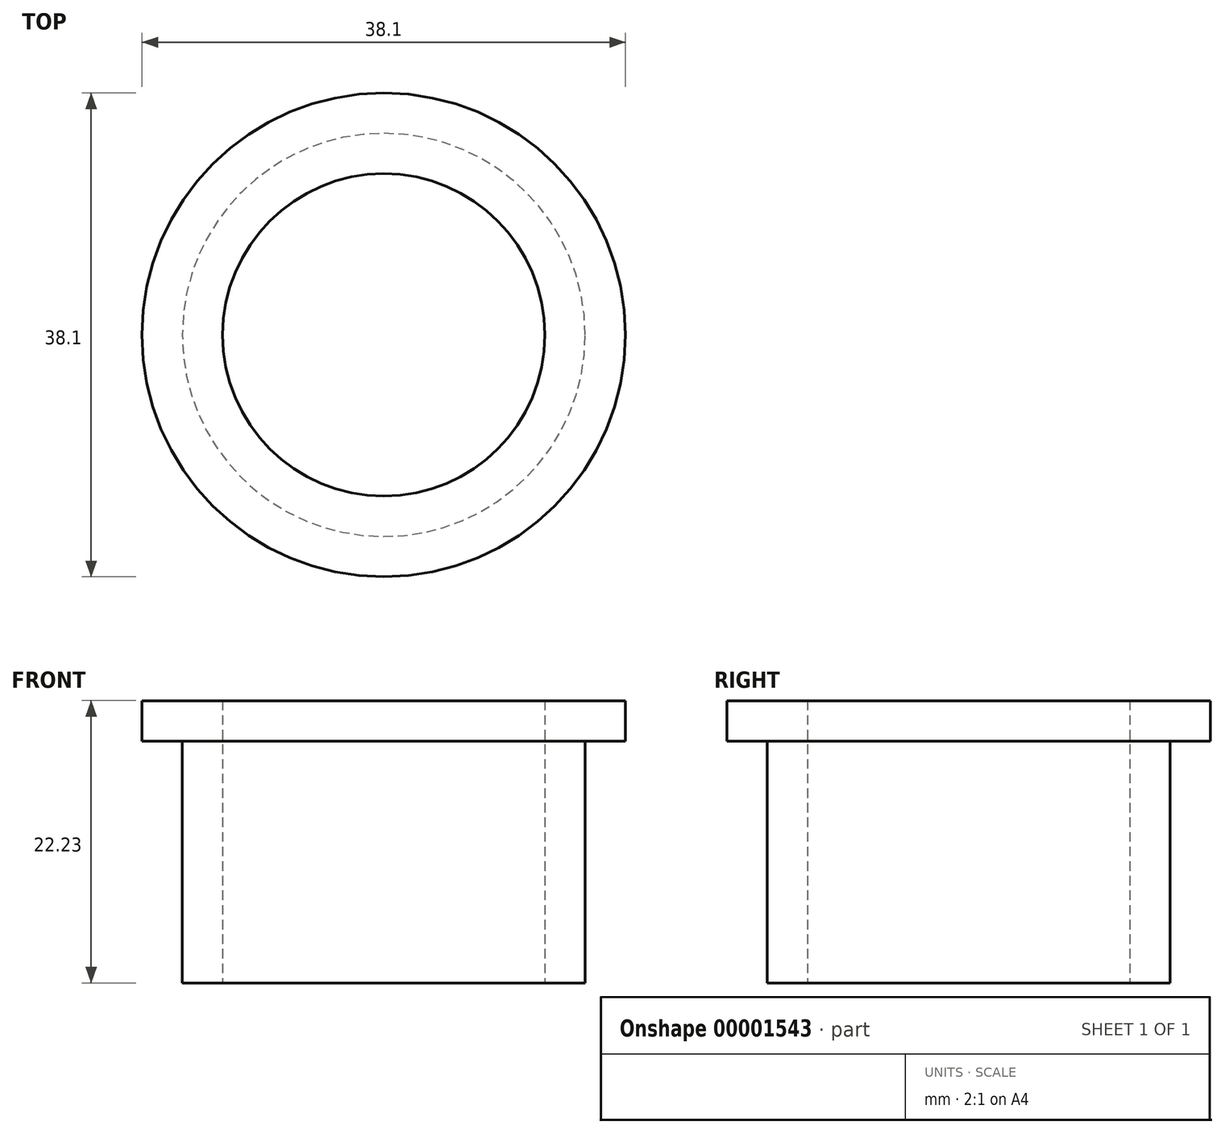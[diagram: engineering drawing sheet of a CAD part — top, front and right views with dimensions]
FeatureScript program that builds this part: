
annotation { "Feature Type Name" : "Feature", "Feature Type Description" : "" }
export const myFeature = defineFeature(function(context is Context, id is Id, definition is map)
    precondition{}
    {
        {
            var Q0;
            Q0=qCreatedBy(makeId("Top.planeOp"),FACE);
            var sketch = newSketch(context, id + "F0", { "sketchPlane" : qUnion([Q0])});
            skCircle(sketch, "E0", {"center": v(0, 0) * mm, "radius": 12.7 * mm});
            skCircle(sketch, "E1", {"center": v(0, 0) * mm, "radius": 19.05 * mm});
            skSolve(sketch);
        }
        {
            var Q0;
            Q0=makeQuery(id+"F0.imprint","IMPRINT",FACE,{"disambiguationData":[TD([[makeQuery(id+"F0.imprint","IMPRINT",EDGE,{"derivedFrom":sQuery(id+"F0.wireOp",EDGE,"E0")}),-1.0]])]});
            extrude(context, id + "F1", {"entities" : qUnion([Q0]), "depth" : 3.17 * mm});
        }
        {
            var Q0;
            Q0=qCreatedBy(makeId("Top.planeOp"),FACE);
            var sketch = newSketch(context, id + "F2", { "sketchPlane" : qUnion([Q0])});
            skCircle(sketch, "E2", {"center": v(0, 0) * mm, "radius": 12.7 * mm});
            skCircle(sketch, "E3", {"center": v(0, 0) * mm, "radius": 15.88 * mm});
            skSolve(sketch);
        }
        {
            var Q0;
            Q0=makeQuery(id+"F2.imprint","IMPRINT",FACE,{"disambiguationData":[TD([[makeQuery(id+"F2.imprint","IMPRINT",EDGE,{"derivedFrom":sQuery(id+"F2.wireOp",EDGE,"E2")}),-1.0]])]});
            extrude(context, id + "F3", {"entities" : qUnion([Q0]), "operationType" : NewBodyOperationType.ADD, "oppositeDirection" : true, "depth" : 19.05 * mm});
        }
    });
